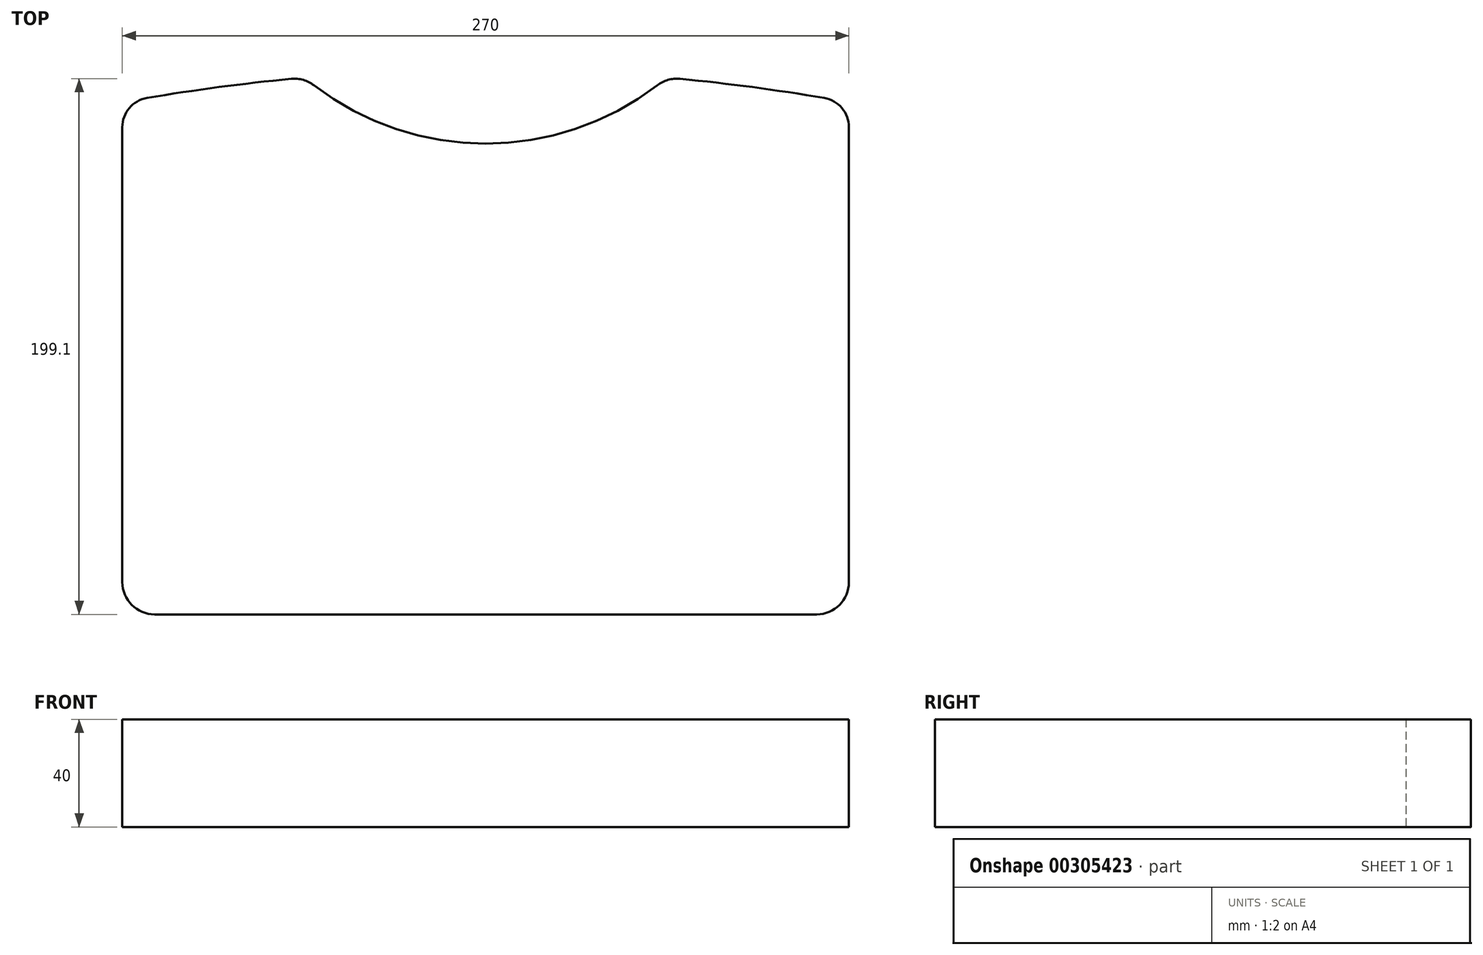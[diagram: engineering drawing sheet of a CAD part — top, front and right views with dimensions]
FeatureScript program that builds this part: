
annotation { "Feature Type Name" : "Feature", "Feature Type Description" : "" }
export const myFeature = defineFeature(function(context is Context, id is Id, definition is map)
    precondition{}
    {
        {
            var Q0;
            Q0=qCreatedBy(makeId("Top.planeOp"),FACE);
            var sketch = newSketch(context, id + "F0", { "sketchPlane" : qUnion([Q0])});
            skLineSegment(sketch, "E0.top", {"start": v(-123, -99.75) * mm, "end": v(123, -99.75) * mm});
            skLineSegment(sketch, "E0.left", {"start": v(-135, 81.33) * mm, "end": v(-135, -87.75) * mm});
            skLineSegment(sketch, "E0.right", {"start": v(135, 81.33) * mm, "end": v(135, -87.75) * mm});
            skLineSegment(sketch, "E1", {"start": v(-173.86, 75.25) * mm, "end": v(164.52, 75.25) * mm, "construction": true});
            skLineSegment(sketch, "E2", {"start": v(-50.1, 180.15) * mm, "end": v(39.06, 180.15) * mm, "construction": true});
            skLineSegment(sketch, "E3", {"start": v(39.06, 180.15) * mm, "end": v(39.06, 177.86) * mm});
            skLineSegment(sketch, "E4", {"start": v(0, 0) * mm, "end": v(0, 180.15) * mm, "construction": true});
            skArc(sketch, "E5", {"start": v(0, 75.25) * mm, "mid": v(-33.68, 80.8) * mm, "end": v(-63.8, 96.88) * mm});
            skArc(sketch, "E6", {"start": v(0, 75.25) * mm, "mid": v(33.68, 80.8) * mm, "end": v(63.8, 96.88) * mm});
            skPoint(sketch, "E7", {"position": v(0, -649.75) * mm});
            skArc(sketch, "E8", {"start": v(125.84, 92.18) * mm, "mid": v(99.1, 96.22) * mm, "end": v(72.24, 99.3) * mm});
            skArc(sketch, "E9.trimOffspring", {"start": v(-72.24, 99.3) * mm, "mid": v(-99.1, 96.22) * mm, "end": v(-125.84, 92.18) * mm});
            skPoint(sketch, "E10.visualSharp", {"position": v(67.38, 99.75) * mm});
            skArc(sketch, "E10.filletArc", {"start": v(72.24, 99.3) * mm, "mid": v(67.8, 98.89) * mm, "end": v(63.8, 96.88) * mm});
            skPoint(sketch, "E11.visualSharp", {"position": v(-67.38, 99.75) * mm});
            skArc(sketch, "E11.filletArc", {"start": v(-63.8, 96.88) * mm, "mid": v(-67.8, 98.89) * mm, "end": v(-72.24, 99.3) * mm});
            skPoint(sketch, "E12.visualSharp", {"position": v(-135, 90.56) * mm});
            skArc(sketch, "E12.filletArc", {"start": v(-125.84, 92.18) * mm, "mid": v(-132.4, 88.43) * mm, "end": v(-135, 81.33) * mm});
            skPoint(sketch, "E13.visualSharp", {"position": v(135, 90.56) * mm});
            skArc(sketch, "E13.filletArc", {"start": v(135, 81.33) * mm, "mid": v(132.4, 88.43) * mm, "end": v(125.84, 92.18) * mm});
            skPoint(sketch, "E14.visualSharp", {"position": v(135, -99.75) * mm});
            skArc(sketch, "E14.filletArc", {"start": v(123, -99.75) * mm, "mid": v(131.49, -96.24) * mm, "end": v(135, -87.75) * mm});
            skPoint(sketch, "E15.visualSharp", {"position": v(-135, -99.75) * mm});
            skArc(sketch, "E15.filletArc", {"start": v(-135, -87.75) * mm, "mid": v(-131.49, -96.24) * mm, "end": v(-123, -99.75) * mm});
            skSolve(sketch);
        }
        {
            var Q0;
            Q0=qSketchRegion(id+"F0",true);
            extrude(context, id + "F1", {"entities" : qUnion([Q0]), "depth" : 40 * mm});
        }
    });
